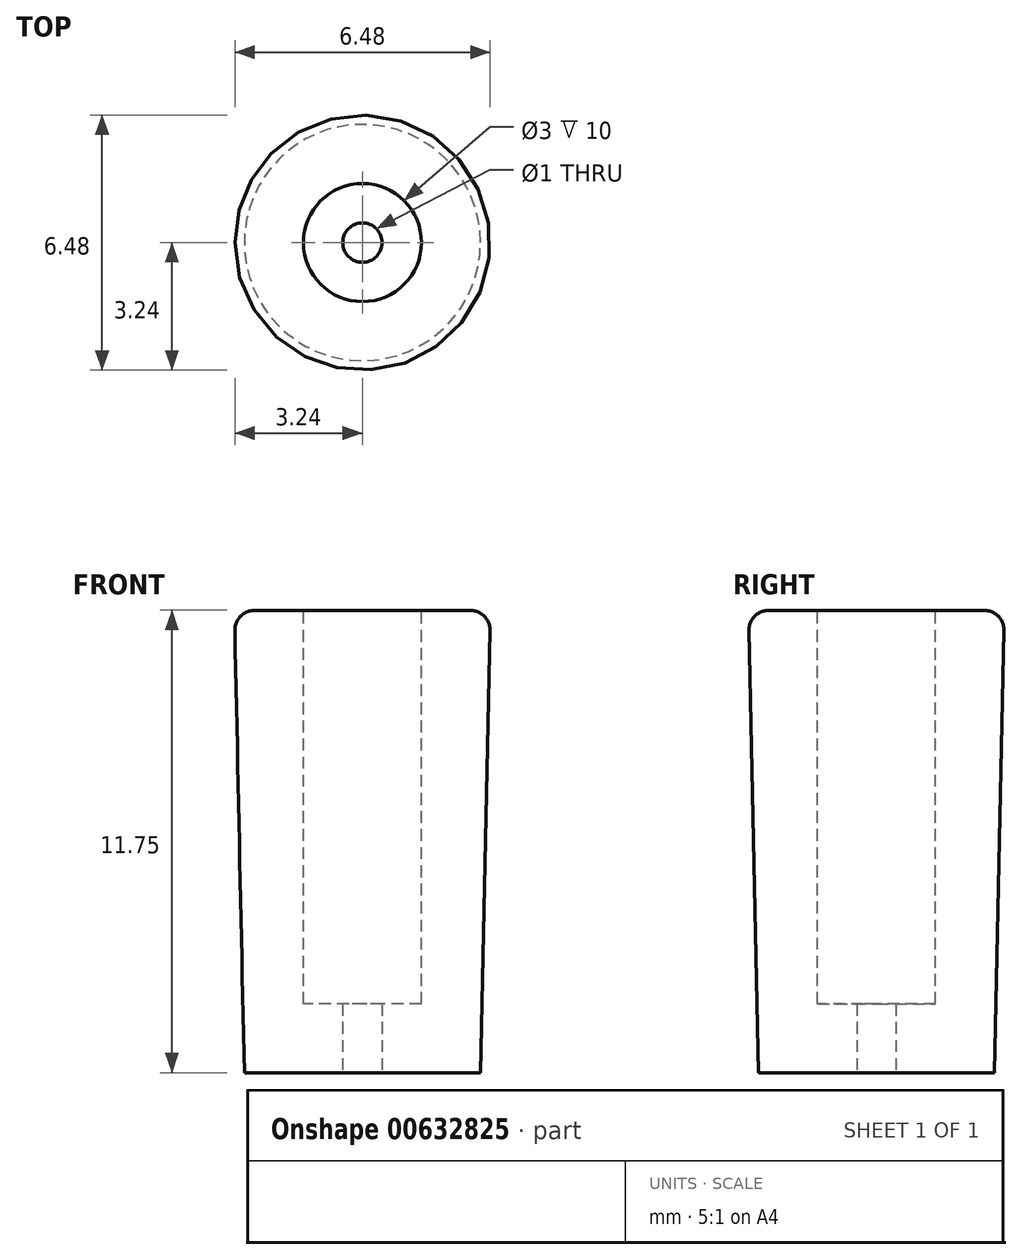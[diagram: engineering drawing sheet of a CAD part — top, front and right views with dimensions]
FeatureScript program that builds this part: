
annotation { "Feature Type Name" : "Feature", "Feature Type Description" : "" }
export const myFeature = defineFeature(function(context is Context, id is Id, definition is map)
    precondition{}
    {
        {
            var Q0;
            Q0=qCreatedBy(makeId("Front.planeOp"),FACE);
            var sketch = newSketch(context, id + "F0", { "sketchPlane" : qUnion([Q0])});
            skLineSegment(sketch, "E0", {"start": v(0, -5.56) * mm, "end": v(0, 6.19) * mm});
            skLineSegment(sketch, "E1", {"start": v(0, 6.19) * mm, "end": v(3.25, 6.19) * mm});
            skLineSegment(sketch, "E2", {"start": v(3.25, 6.19) * mm, "end": v(3, -5.56) * mm});
            skLineSegment(sketch, "E3", {"start": v(3, -5.56) * mm, "end": v(0, -5.56) * mm});
            skSolve(sketch);
        }
        {
            var Q0;
            Q0 = qSketchRegion(id + "F0", true);
            var Q1;
            Q1=sQuery(id+"F0.wireOp",EDGE,"E0");
            revolve(context, id + "F1", {"entities" : qUnion([Q0]), "axis" : qUnion([Q1]), "revolveType" : RevolveType.FULL});
        }
        {
            var Q0;
            Q0=makeQuery(id+"F1.opRevolve","SWEPT_EDGE",EDGE,{"disambiguationData":[OSD([sQuery(id+"F0.wireOp",EDGE,"E1"),sQuery(id+"F0.wireOp",EDGE,"E2")])]});
            fillet(context, id + "F2", {"entities" : qUnion([Q0]), "radius" : .5 * mm, "tangentPropagation" : true, "allowEdgeOverflow" : false});
        }
        {
            var Q0;
            Q0=makeQuery(id+"F1.opRevolve","SWEPT_FACE",FACE,{"disambiguationData":[OSD([sQuery(id+"F0.wireOp",EDGE,"E1")])]});
            var sketch = newSketch(context, id + "F3", { "sketchPlane" : qUnion([Q0])});
            skCircle(sketch, "E4", {"center": v(0, 0) * mm, "radius": 1.5 * mm});
            skSolve(sketch);
        }
        {
            var Q0;
            Q0 = qSketchRegion(id + "F3", true);
            extrude(context, id + "F4", {"entities" : qUnion([Q0]), "operationType" : NewBodyOperationType.REMOVE, "oppositeDirection" : true, "depth" : 10 * mm, "offsetDistance" : 25 * mm});
        }
        {
            var Q0;
            Q0=makeQuery(id+"F1.opRevolve","SWEPT_FACE",FACE,{"disambiguationData":[OSD([sQuery(id+"F0.wireOp",EDGE,"E3")])]});
            var sketch = newSketch(context, id + "F5", { "sketchPlane" : qUnion([Q0])});
            skCircle(sketch, "E5", {"center": v(0, 0) * mm, "radius": 0.5 * mm});
            skSolve(sketch);
        }
        {
            var Q0;
            Q0 = qSketchRegion(id + "F5", true);
            extrude(context, id + "F6", {"entities" : qUnion([Q0]), "operationType" : NewBodyOperationType.REMOVE, "oppositeDirection" : true, "depth" : 2 * mm, "offsetDistance" : 25 * mm});
        }
    });
